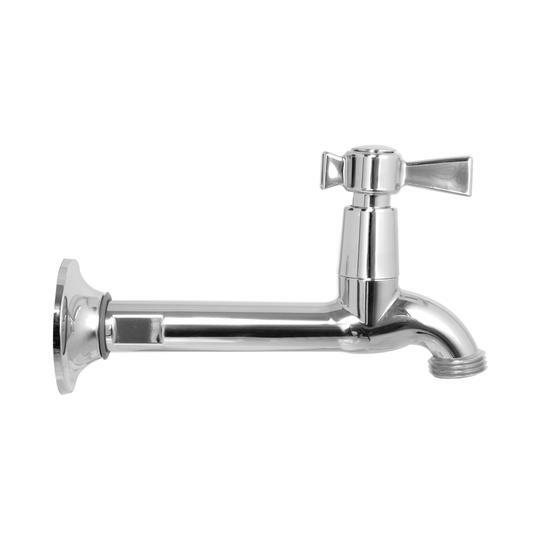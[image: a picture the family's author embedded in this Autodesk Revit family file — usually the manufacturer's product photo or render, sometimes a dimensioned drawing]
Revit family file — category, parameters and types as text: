
# Revit family: 01-2992-11 LLAVE EXTENSION PLASTICA MANGUERA CROMO
name_source: partatom
category: Plumbing Fixtures
revit_build: Autodesk Revit 2018 (Build: 20170223_1515(x64)
units: mm (PartAtom-declared; Revit-internal decimal feet)

## family parameters
Cut with Voids When Loaded = No
Host = Face
OmniClass Number = 23.31.11.00
Part Type = Normal
Room Calculation Point = No
Round Connector Dimension = Use Diameter
Shared = No

## types (1)
- 01-2992-11
    Acometida = Dim 1/2" NPT
    Alto = 107 mm  [stored 0.35105 ft]
    Ancho = 199.4 mm  [stored 0.654199 ft]
    Ancho manija llave = 67 mm
    CW Connection = Yes
    Default Elevation = 0 mm  [stored 0 ft]
    Description = Llave jardin
    Dim Escudo = 60 mm
    HW Connection = Yes
    Link Ficha Tecnica = http://infotecnica.gricol.com
    Manufacturer = Gricol
    Model = 01-2992-11
    Plastico - ABS Cromado = Plastico - ABS Cromado
    Product Name = LLAVE MANGUERA PLASTICA CROMO
    Salida = Dim 3/4" NH
    Type Image = <None>
    URL = https://www.gricol.com
    Vent Connection = No
    Waste Connection = No

note: [stored X ft] marks values corroborated as IEEE doubles in the binary element streams (Revit-internal decimal feet)

## geometry (parser evidence)
native form markers: Blend x2, Sweep x3
no freeform markers — native parametric forms only
